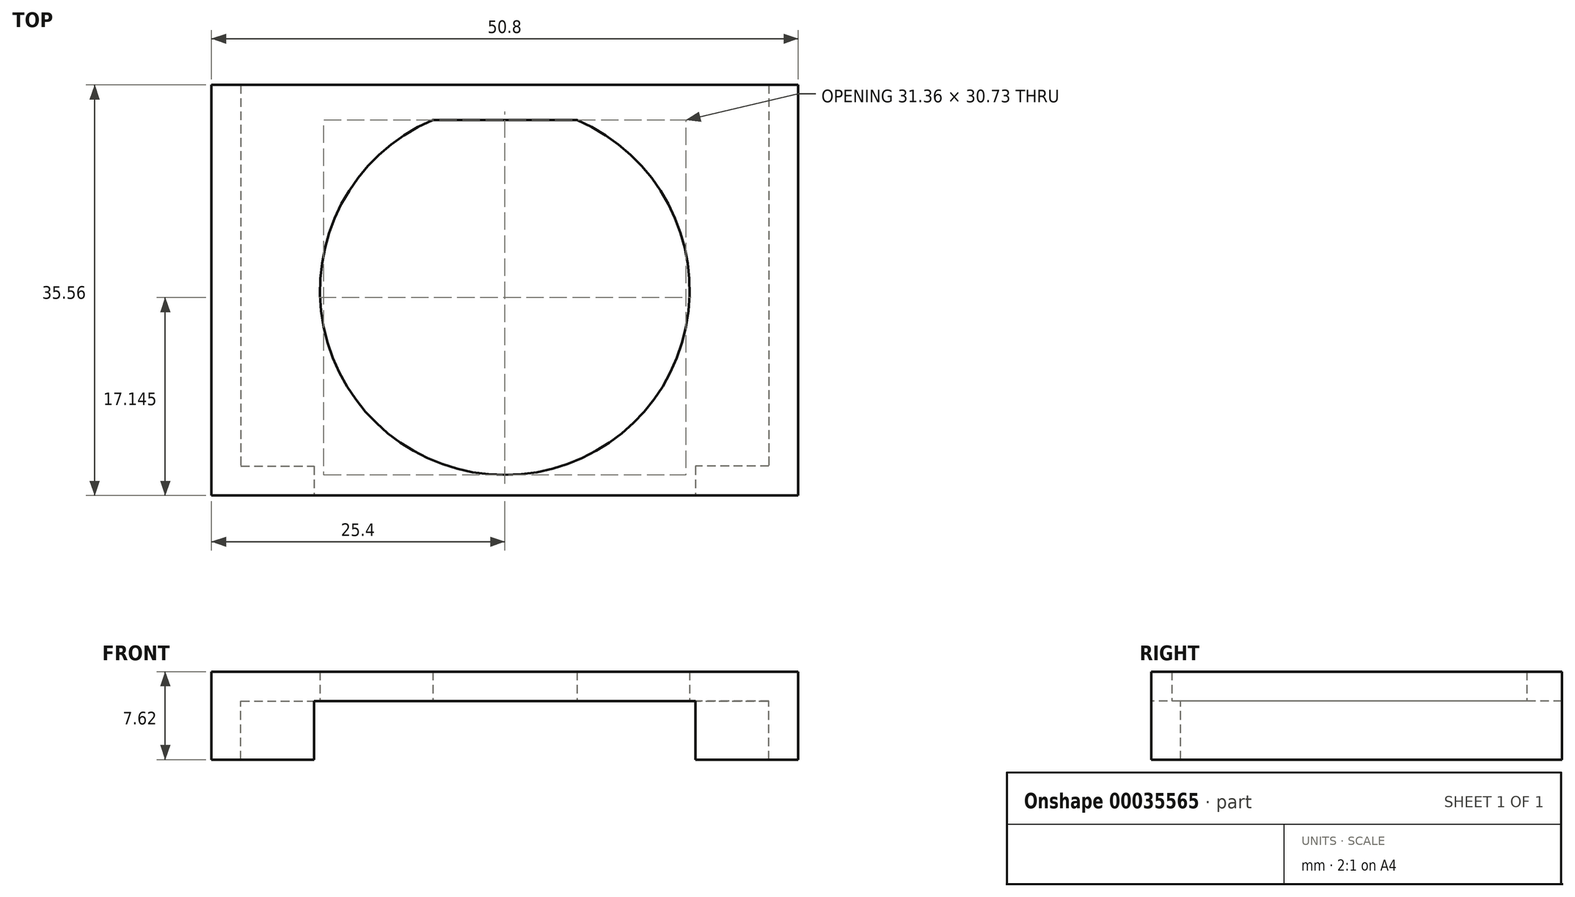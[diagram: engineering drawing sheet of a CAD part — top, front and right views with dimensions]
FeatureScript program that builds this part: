
annotation { "Feature Type Name" : "Feature", "Feature Type Description" : "" }
export const myFeature = defineFeature(function(context is Context, id is Id, definition is map)
    precondition{}
    {
        {
            var Q0;
            Q0=qCreatedBy(makeId("Top.planeOp"),FACE);
            var sketch = newSketch(context, id + "F0", { "sketchPlane" : qUnion([Q0])});
            skLineSegment(sketch, "E0.rect.bottom", {"start": v(-25.4, 17.78) * mm, "end": v(25.4, 17.78) * mm});
            skLineSegment(sketch, "E0.rect.top", {"start": v(-25.4, -17.78) * mm, "end": v(25.4, -17.78) * mm});
            skLineSegment(sketch, "E0.rect.left", {"start": v(-25.4, 17.78) * mm, "end": v(-25.4, -17.78) * mm});
            skLineSegment(sketch, "E0.rect.right", {"start": v(25.4, 17.78) * mm, "end": v(25.4, -17.78) * mm});
            skPoint(sketch, "E0.rect.middle", {"position": v(0, 0) * mm});
            skArc(sketch, "E1", {"start": v(-6.25, 14.73) * mm, "mid": v(0, -16) * mm, "end": v(6.25, 14.73) * mm});
            skLineSegment(sketch, "E2", {"start": v(-6.25, 14.73) * mm, "end": v(6.25, 14.73) * mm});
            skSolve(sketch);
        }
        {
            var Q0;
            Q0 = qSketchRegion(id + "F0", true);
            extrude(context, id + "F1", {"entities" : qUnion([Q0]), "depth" : 2.54 * mm});
        }
        {
            var Q0;
            Q0=makeQuery(id+"F1.opExtrude","CAP_FACE",FACE,{"disambiguationData":[OSD([sQuery(id+"F0.wireOp",EDGE,"E0.rect.bottom"),sQuery(id+"F0.wireOp",EDGE,"E0.rect.top"),sQuery(id+"F0.wireOp",EDGE,"E0.rect.left"),sQuery(id+"F0.wireOp",EDGE,"E0.rect.right"),sQuery(id+"F0.wireOp",EDGE,"E1")])],"isStart":true});
            var sketch = newSketch(context, id + "F2", { "sketchPlane" : qUnion([Q0])});
            skLineSegment(sketch, "E3", {"start": v(-22.86, -17.78) * mm, "end": v(-22.86, 15.24) * mm});
            skLineSegment(sketch, "E4", {"start": v(-22.86, 15.24) * mm, "end": v(-16.51, 15.24) * mm});
            skLineSegment(sketch, "E5", {"start": v(-16.51, 15.24) * mm, "end": v(-16.51, 17.78) * mm});
            skLineSegment(sketch, "E6", {"start": v(-16.51, 17.78) * mm, "end": v(-25.4, 17.78) * mm});
            skLineSegment(sketch, "E7", {"start": v(-25.4, 17.78) * mm, "end": v(-25.4, -17.78) * mm});
            skLineSegment(sketch, "E8", {"start": v(-25.4, -17.78) * mm, "end": v(-22.86, -17.78) * mm});
            skLineSegment(sketch, "E9.MirrorCS", {"start": v(25.4, -17.78) * mm, "end": v(22.86, -17.78) * mm});
            skLineSegment(sketch, "E10.MirrorCS", {"start": v(22.86, -17.78) * mm, "end": v(22.86, 15.24) * mm});
            skLineSegment(sketch, "E11.MirrorCS", {"start": v(22.86, 15.24) * mm, "end": v(16.51, 15.24) * mm});
            skLineSegment(sketch, "E12.MirrorCS", {"start": v(16.51, 15.24) * mm, "end": v(16.51, 17.78) * mm});
            skLineSegment(sketch, "E13.MirrorCS", {"start": v(16.51, 17.78) * mm, "end": v(25.4, 17.78) * mm});
            skLineSegment(sketch, "E14.MirrorCS", {"start": v(25.4, 17.78) * mm, "end": v(25.4, -17.78) * mm});
            skSolve(sketch);
        }
        {
            var Q0;
            Q0 = qSketchRegion(id + "F2", true);
            extrude(context, id + "F3", {"entities" : qUnion([Q0]), "operationType" : NewBodyOperationType.ADD, "depth" : 5.08 * mm});
        }
    });
